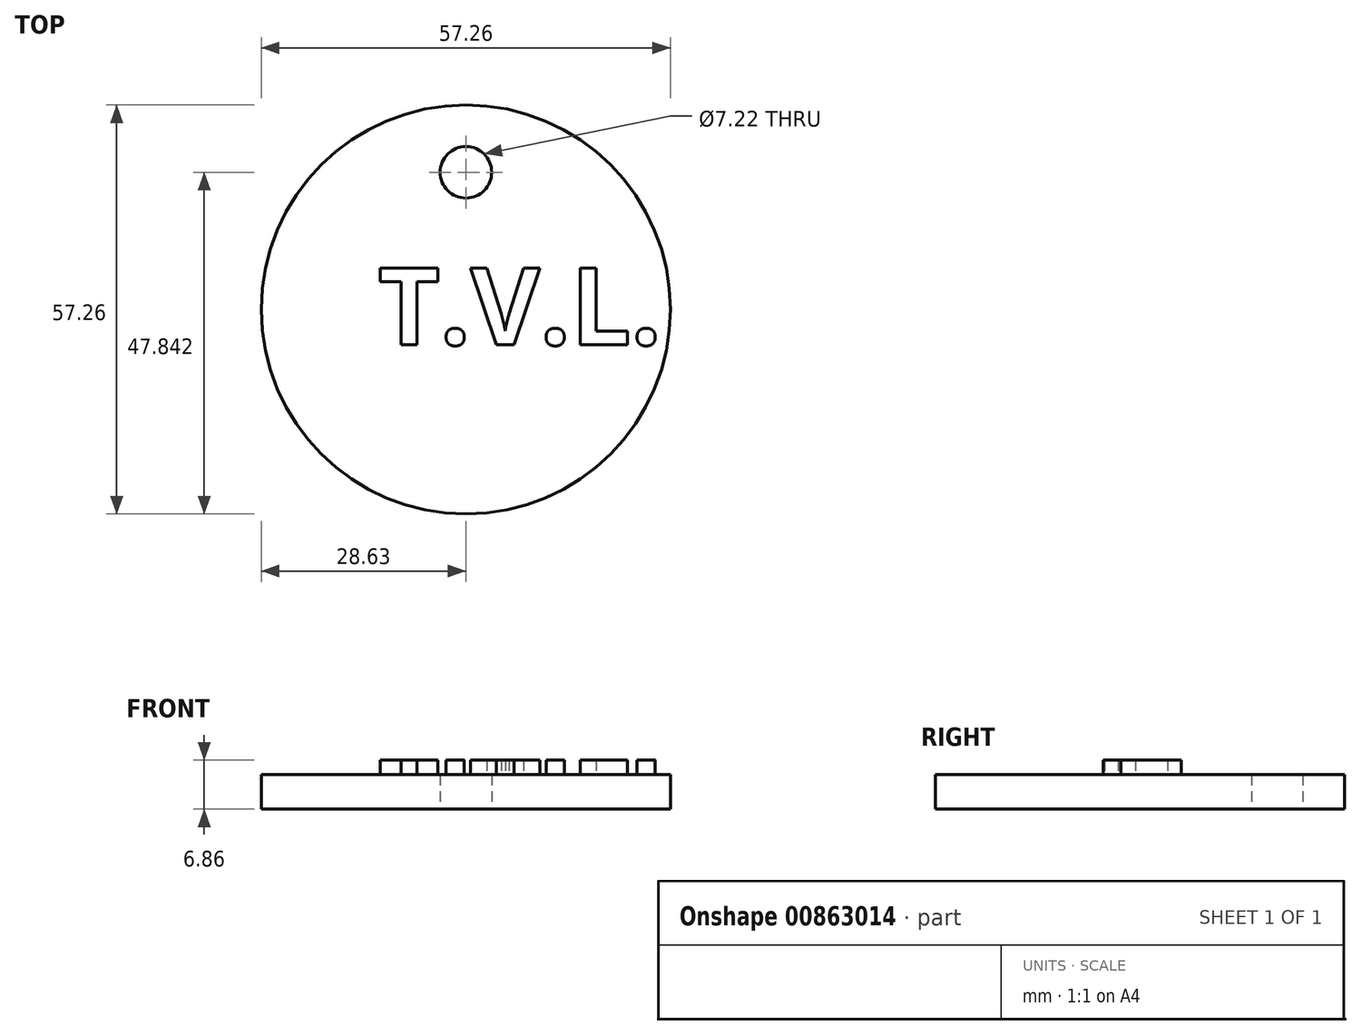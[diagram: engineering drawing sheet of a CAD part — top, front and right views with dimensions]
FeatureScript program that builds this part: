
annotation { "Feature Type Name" : "Feature", "Feature Type Description" : "" }
export const myFeature = defineFeature(function(context is Context, id is Id, definition is map)
    precondition{}
    {
        {
            var Q0;
            Q0=qCreatedBy(makeId("Top.planeOp"),FACE);
            var sketch = newSketch(context, id + "F0", { "sketchPlane" : qUnion([Q0])});
            skCircle(sketch, "E0", {"center": v(0, 0) * mm, "radius": 28.63 * mm});
            skCircle(sketch, "E1", {"center": v(0, 19.21) * mm, "radius": 3.6 * mm});
            skSolve(sketch);
        }
        {
            var Q0;
            Q0 = qSketchRegion(id + "F0", true);
            extrude(context, id + "F1", {"entities" : qUnion([Q0]), "depth" : 4.83 * mm, "offsetDistance" : 25.4 * mm});
        }
        {
            var Q0;
            Q0=qCreatedBy(makeId("Top.planeOp"),FACE);
            var sketch = newSketch(context, id + "F2", { "sketchPlane" : qUnion([Q0])});
            skText(sketch, "E2", { "text": "T.V.L.", "fontName": "OpenSans-Bold.ttf"});
            const initialGuessF2  = {"E2": [-0.0123, -0.00492, 1, 0, 0.01078]};
            skSetInitialGuess(sketch, initialGuessF2);
            skSolve(sketch);
        }
        {
            var Q0;
            Q0 = qSketchRegion(id + "F2", true);
            extrude(context, id + "F3", {"entities" : qUnion([Q0]), "operationType" : NewBodyOperationType.ADD, "depth" : 6.86 * mm, "offsetDistance" : 25.4 * mm});
        }
    });
